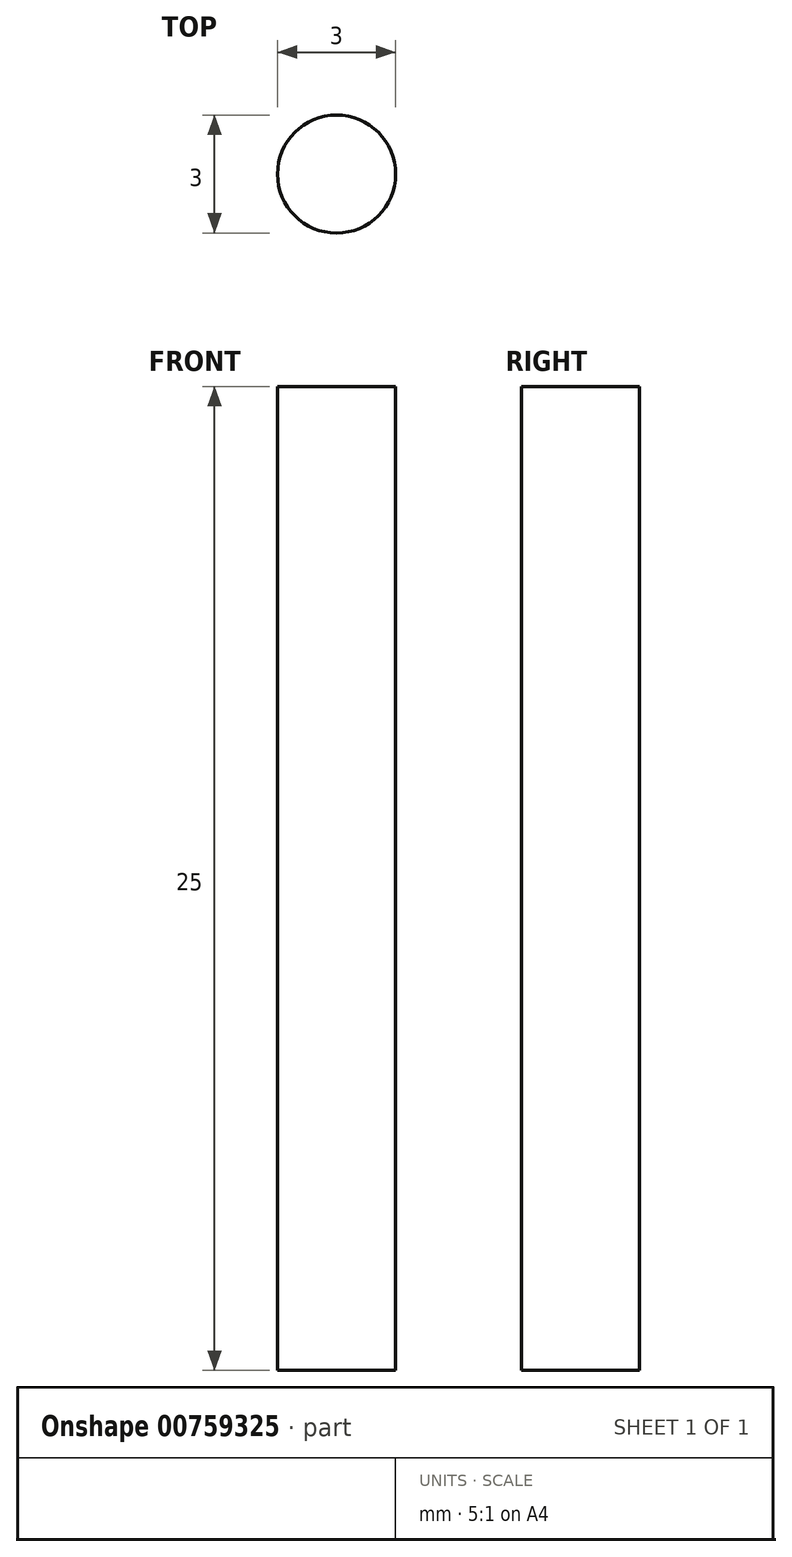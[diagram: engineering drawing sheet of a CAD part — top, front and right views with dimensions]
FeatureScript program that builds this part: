
annotation { "Feature Type Name" : "Feature", "Feature Type Description" : "" }
export const myFeature = defineFeature(function(context is Context, id is Id, definition is map)
    precondition{}
    {
        {
            var Q0;
            Q0=qCreatedBy(makeId("Top.planeOp"),FACE);
            var sketch = newSketch(context, id + "F0", { "sketchPlane" : qUnion([Q0])});
            skCircle(sketch, "E0", {"center": v(0, 0) * mm, "radius": 1.5 * mm});
            skSolve(sketch);
        }
        {
            var Q0;
            Q0=makeQuery(id+"F0.imprint","IMPRINT",FACE,{"disambiguationData":[TD([[makeQuery(id+"F0.imprint","IMPRINT",EDGE,{"derivedFrom":sQuery(id+"F0.wireOp",EDGE,"E0")}),1.0]])]});
            extrude(context, id + "F1", {"entities" : qUnion([Q0]), "depth" : 25 * mm, "offsetDistance" : 25 * mm});
        }
    });
